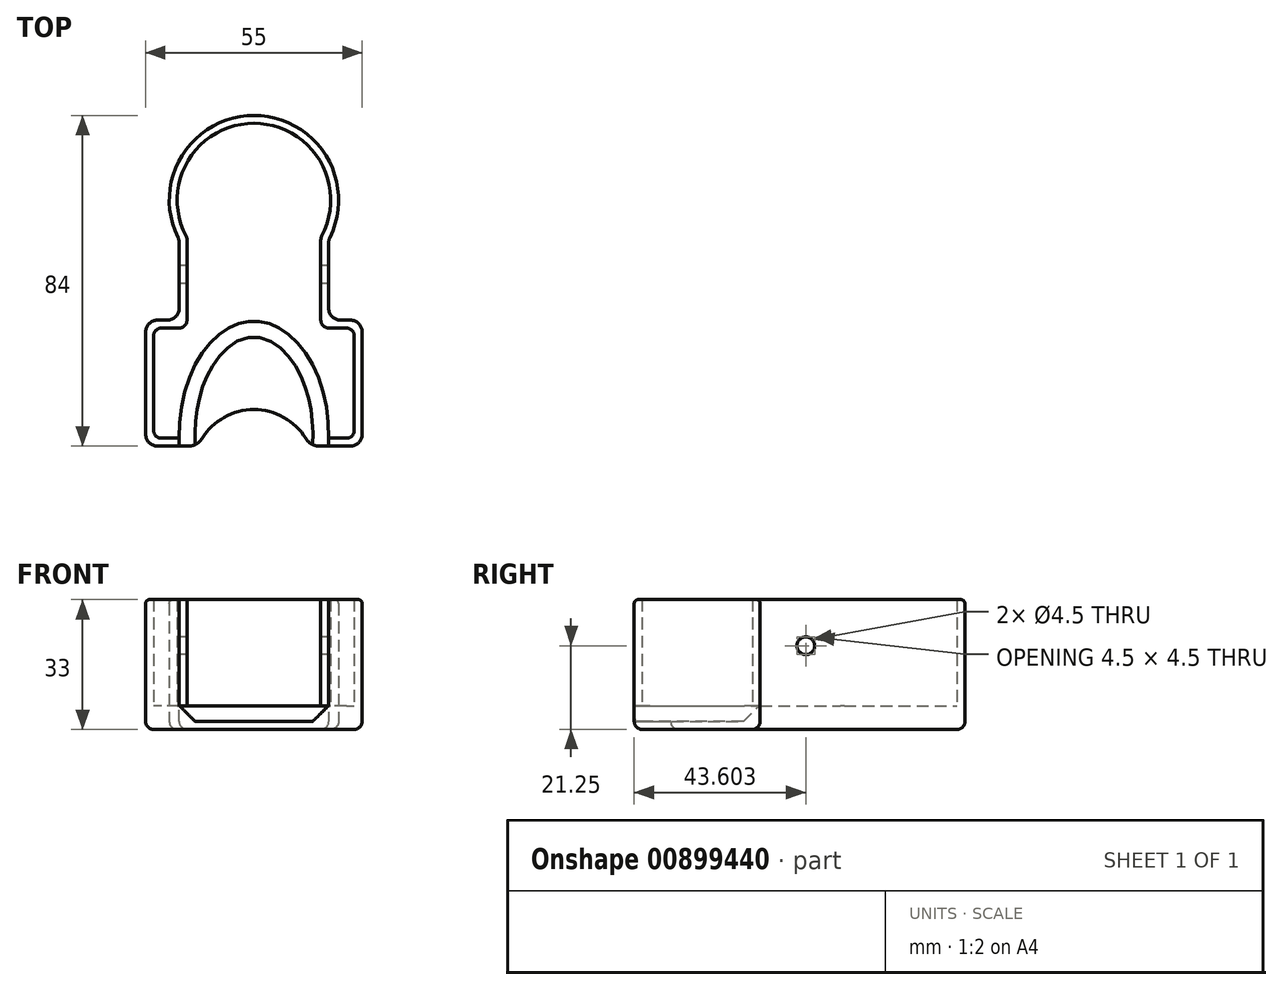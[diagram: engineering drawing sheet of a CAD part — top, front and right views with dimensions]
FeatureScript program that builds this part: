
annotation { "Feature Type Name" : "Feature", "Feature Type Description" : "" }
export const myFeature = defineFeature(function(context is Context, id is Id, definition is map)
    precondition{}
    {
        {
            var Q0;
            Q0=qCreatedBy(makeId("Top.planeOp"),FACE);
            var sketch = newSketch(context, id + "F0", { "sketchPlane" : qUnion([Q0])});
            skArc(sketch, "E0", {"start": v(17, -9.55) * mm, "mid": v(0, 19.5) * mm, "end": v(-17, -9.55) * mm});
            skArc(sketch, "E1", {"start": v(19, -10.06) * mm, "mid": v(0, 21.5) * mm, "end": v(-19, -10.06) * mm});
            skPoint(sketch, "E2.middle", {"position": v(0, -23.16) * mm});
            skLineSegment(sketch, "E3.left", {"start": v(19, -10.06) * mm, "end": v(19, -30.5) * mm});
            skLineSegment(sketch, "E3.right", {"start": v(-19, -10.06) * mm, "end": v(-19, -30.5) * mm});
            skLineSegment(sketch, "E4.bottom", {"start": v(27.5, -30.5) * mm, "end": v(19, -30.5) * mm});
            skLineSegment(sketch, "E4.top", {"start": v(27.5, -62.5) * mm, "end": v(-27.5, -62.5) * mm});
            skLineSegment(sketch, "E4.left", {"start": v(27.5, -30.5) * mm, "end": v(27.5, -62.5) * mm});
            skLineSegment(sketch, "E4.right", {"start": v(-27.5, -30.5) * mm, "end": v(-27.5, -62.5) * mm});
            skPoint(sketch, "E4.middle", {"position": v(0, -46.5) * mm});
            skLineSegment(sketch, "E5", {"start": v(-39.92, 21.5) * mm, "end": v(44.93, 21.5) * mm, "construction": true});
            skLineSegment(sketch, "E6.bottom", {"start": v(25.5, -60.5) * mm, "end": v(-25.5, -60.5) * mm});
            skLineSegment(sketch, "E6.top", {"start": v(25.5, -32.5) * mm, "end": v(17, -32.5) * mm});
            skLineSegment(sketch, "E6.left", {"start": v(25.5, -60.5) * mm, "end": v(25.5, -32.5) * mm});
            skLineSegment(sketch, "E6.right", {"start": v(-25.5, -60.5) * mm, "end": v(-25.5, -32.5) * mm});
            skLineSegment(sketch, "E7.trimOffspring", {"start": v(-19, -30.5) * mm, "end": v(-27.5, -30.5) * mm});
            skLineSegment(sketch, "E8.trimOffspring", {"start": v(-17, -32.5) * mm, "end": v(-25.5, -32.5) * mm});
            skLineSegment(sketch, "E9", {"start": v(-17, -32.5) * mm, "end": v(-17, -9.55) * mm});
            skLineSegment(sketch, "E10", {"start": v(17, -32.5) * mm, "end": v(17, -9.55) * mm});
            skSolve(sketch);
        }
        {
            var Q0;
            Q0 = qSketchRegion(id + "F0", true);
            extrude(context, id + "F1", {"entities" : qUnion([Q0]), "depth" : 27 * mm, "offsetDistance" : 25 * mm});
        }
        {
            var Q0;
            Q0=qCreatedBy(makeId("Top.planeOp"),FACE);
            var sketch = newSketch(context, id + "F2", { "sketchPlane" : qUnion([Q0])});
            skArc(sketch, "E11", {"start": v(19, -10.06) * mm, "mid": v(0, 21.5) * mm, "end": v(-19, -10.06) * mm});
            skPoint(sketch, "E12.middle", {"position": v(0, -23.16) * mm});
            skLineSegment(sketch, "E13.left", {"start": v(19, -10.06) * mm, "end": v(19, -30.5) * mm});
            skLineSegment(sketch, "E13.right", {"start": v(-19, -10.06) * mm, "end": v(-19, -30.5) * mm});
            skLineSegment(sketch, "E14.bottom", {"start": v(27.5, -30.5) * mm, "end": v(19, -30.5) * mm});
            skLineSegment(sketch, "E14.top", {"start": v(27.5, -62.5) * mm, "end": v(-27.5, -62.5) * mm});
            skLineSegment(sketch, "E14.left", {"start": v(27.5, -30.5) * mm, "end": v(27.5, -62.5) * mm});
            skLineSegment(sketch, "E14.right", {"start": v(-27.5, -30.5) * mm, "end": v(-27.5, -62.5) * mm});
            skPoint(sketch, "E14.middle", {"position": v(0, -46.5) * mm});
            skLineSegment(sketch, "E15.trimOffspring", {"start": v(-19, -30.5) * mm, "end": v(-27.5, -30.5) * mm});
            skSolve(sketch);
        }
        {
            var Q0;
            Q0 = qSketchRegion(id + "F2", true);
            extrude(context, id + "F3", {"entities" : qUnion([Q0]), "operationType" : NewBodyOperationType.ADD, "oppositeDirection" : true, "depth" : 6 * mm, "offsetDistance" : 25 * mm});
        }
        {
            var Q0;
            Q0=qCreatedBy(makeId("Top.planeOp"),FACE);
            var sketch = newSketch(context, id + "F4", { "sketchPlane" : qUnion([Q0])});
            skLineSegment(sketch, "E16", {"start": v(49.02, 21.5) * mm, "end": v(-41.67, 21.5) * mm, "construction": true});
            skEllipse(sketch, "E17", {"center": v(0, -60) * mm, "majorRadius": 31 * mm, "minorRadius": 21 * mm, "majorAxis": v(0, 1)});
            skSolve(sketch);
        }
        {
            var Q0;
            Q0 = qSketchRegion(id + "F4", true);
            extrude(context, id + "F5", {"entities" : qUnion([Q0]), "operationType" : NewBodyOperationType.ADD, "oppositeDirection" : true, "depth" : 6 * mm, "offsetDistance" : 25 * mm});
        }
        {
            var Q0;
            Q0=qCreatedBy(makeId("Top.planeOp"),FACE);
            var sketch = newSketch(context, id + "F6", { "sketchPlane" : qUnion([Q0])});
            skEllipse(sketch, "E18", {"center": v(0, -59.78) * mm, "majorRadius": 29 * mm, "minorRadius": 19 * mm, "majorAxis": v(0, 1)});
            skSolve(sketch);
        }
        {
            var Q0;
            Q0 = qSketchRegion(id + "F6", true);
            extrude(context, id + "F7", {"entities" : qUnion([Q0]), "operationType" : NewBodyOperationType.REMOVE, "oppositeDirection" : true, "depth" : 4 * mm, "offsetDistance" : 25 * mm});
        }
        {
            var Q0;
            Q0=makeQuery(id+"F7.boolean.opBoolean","COPY",EDGE,{"derivedFrom":makeQuery(id+"F7.opExtrude","CAP_EDGE",EDGE,{"disambiguationData":[OSD([sQuery(id+"F6.wireOp",EDGE,"E18")])],"isStart":false})});
            chamfer(context, id + "F8", {"entities" : qUnion([Q0]), "width" : 4 * mm, "tangentPropagation" : true});
        }
        {
            var Q0;
            Q0=makeQuery(id+"F5.opExtrude","CAP_EDGE",EDGE,{"disambiguationData":[OSD([sQuery(id+"F4.wireOp",EDGE,"E17")])],"isStart":false});
            chamfer(context, id + "F9", {"entities" : qUnion([Q0]), "width" : 6 * mm, "tangentPropagation" : true});
        }
        {
            var Q0;
            Q0=qCreatedBy(makeId("Top.planeOp"),FACE);
            var sketch = newSketch(context, id + "F10", { "sketchPlane" : qUnion([Q0])});
            skLineSegment(sketch, "E19", {"start": v(-36.83, 21.5) * mm, "end": v(59.05, 21.5) * mm, "construction": true});
            skLineSegment(sketch, "E20.bottom", {"start": v(-18.92, -94.76) * mm, "end": v(18.92, -94.76) * mm});
            skLineSegment(sketch, "E20.left", {"start": v(-18.92, -94.76) * mm, "end": v(-18.92, -62.5) * mm});
            skLineSegment(sketch, "E20.right", {"start": v(18.92, -94.76) * mm, "end": v(18.92, -62.5) * mm});
            skPoint(sketch, "E20.middle", {"position": v(0, -78.63) * mm});
            skLineSegment(sketch, "E21.bottom", {"start": v(18.92, -62.5) * mm, "end": v(-18.92, -62.5) * mm});
            skLineSegment(sketch, "E22.bottom", {"start": v(18.92, -62.5) * mm, "end": v(22.92, -62.5) * mm});
            skLineSegment(sketch, "E22.top", {"start": v(18.92, -75.28) * mm, "end": v(22.92, -75.28) * mm});
            skLineSegment(sketch, "E22.left", {"start": v(18.92, -62.5) * mm, "end": v(18.92, -75.28) * mm});
            skLineSegment(sketch, "E22.right", {"start": v(22.92, -62.5) * mm, "end": v(22.92, -75.28) * mm});
            skLineSegment(sketch, "E23.bottom", {"start": v(-18.92, -62.5) * mm, "end": v(-22.65, -62.5) * mm});
            skLineSegment(sketch, "E23.top", {"start": v(-18.92, -75.28) * mm, "end": v(-22.65, -75.28) * mm});
            skLineSegment(sketch, "E23.left", {"start": v(-18.92, -62.5) * mm, "end": v(-18.92, -75.28) * mm});
            skLineSegment(sketch, "E23.right", {"start": v(-22.65, -62.5) * mm, "end": v(-22.65, -75.28) * mm});
            skSolve(sketch);
        }
        {
            var Q0;
            Q0 = qSketchRegion(id + "F10", true);
            var Q1;
            Q1=makeQuery(id+"F3.opExtrude","CAP_FACE",FACE,{"disambiguationData":[OSD([sQuery(id+"F2.wireOp",EDGE,"E11"),sQuery(id+"F2.wireOp",EDGE,"E13.left"),sQuery(id+"F2.wireOp",EDGE,"E13.right"),sQuery(id+"F2.wireOp",EDGE,"E14.bottom"),sQuery(id+"F2.wireOp",EDGE,"E14.top"),sQuery(id+"F2.wireOp",EDGE,"E14.left"),sQuery(id+"F2.wireOp",EDGE,"E14.right"),sQuery(id+"F2.wireOp",EDGE,"E15.trimOffspring")])],"isStart":false});
            var Q2;
            Q2=makeQuery(id+"F1.opExtrude","CAP_FACE",FACE,{"disambiguationData":[OSD([sQuery(id+"F0.wireOp",EDGE,"E0"),sQuery(id+"F0.wireOp",EDGE,"E1"),sQuery(id+"F0.wireOp",EDGE,"E3.left"),sQuery(id+"F0.wireOp",EDGE,"E3.right"),sQuery(id+"F0.wireOp",EDGE,"E4.bottom"),sQuery(id+"F0.wireOp",EDGE,"E4.top"),sQuery(id+"F0.wireOp",EDGE,"E4.left"),sQuery(id+"F0.wireOp",EDGE,"E4.right"),sQuery(id+"F0.wireOp",EDGE,"E6.bottom"),sQuery(id+"F0.wireOp",EDGE,"E6.top"),sQuery(id+"F0.wireOp",EDGE,"E6.left"),sQuery(id+"F0.wireOp",EDGE,"E6.right"),sQuery(id+"F0.wireOp",EDGE,"E7.trimOffspring"),sQuery(id+"F0.wireOp",EDGE,"E8.trimOffspring"),sQuery(id+"F0.wireOp",EDGE,"E9"),sQuery(id+"F0.wireOp",EDGE,"E10")])],"isStart":false});
            extrude(context, id + "F11", {"entities" : qUnion([Q0]), "operationType" : NewBodyOperationType.REMOVE, "oppositeDirection" : true, "depth" : 25 * mm, "endBoundEntityFace" : qUnion([Q1]), "offsetDistance" : 25 * mm, "hasSecondDirection" : true, "secondDirectionOppositeDirection" : false, "secondDirectionDepth" : 30 * mm, "secondDirectionBoundEntityFace" : qUnion([Q2])});
        }
        {
            var Q0;
            Q0=qCreatedBy(makeId("Top.planeOp"),FACE);
            var sketch = newSketch(context, id + "F12", { "sketchPlane" : qUnion([Q0])});
            skLineSegment(sketch, "E24.bottom", {"start": v(-19, -60.5) * mm, "end": v(19, -60.5) * mm});
            skLineSegment(sketch, "E24.top", {"start": v(-19, -62.5) * mm, "end": v(19, -62.5) * mm});
            skLineSegment(sketch, "E24.left", {"start": v(-19, -60.5) * mm, "end": v(-19, -62.5) * mm});
            skLineSegment(sketch, "E24.right", {"start": v(19, -60.5) * mm, "end": v(19, -62.5) * mm});
            skPoint(sketch, "E24.middle", {"position": v(0, -61.5) * mm});
            skSolve(sketch);
        }
        {
            var Q0;
            Q0 = qSketchRegion(id + "F12", true);
            extrude(context, id + "F13", {"entities" : qUnion([Q0]), "operationType" : NewBodyOperationType.REMOVE, "depth" : 30 * mm, "offsetDistance" : 25 * mm});
        }
        {
            var Q0;
            Q0=makeQuery(id+"F5.opExtrude","CAP_FACE",FACE,{"disambiguationData":[OSD([sQuery(id+"F4.wireOp",EDGE,"E17")])],"isStart":false});
            var sketch = newSketch(context, id + "F14", { "sketchPlane" : qUnion([Q0])});
            skCircle(sketch, "E25", {"center": v(0, 68.72) * mm, "radius": 15.5 * mm});
            skLineSegment(sketch, "E26", {"start": v(-15.5, 16.16) * mm, "end": v(-15.5, 72.02) * mm, "construction": true});
            skSolve(sketch);
        }
        {
            var Q0;
            Q0 = qSketchRegion(id + "F14", true);
            var Q1;
            Q1=makeQuery(id+"F7.boolean.opBoolean","COPY",FACE,{"derivedFrom":makeQuery(id+"F7.opExtrude","CAP_FACE",FACE,{"disambiguationData":[OSD([sQuery(id+"F6.wireOp",EDGE,"E18")])],"isStart":false})});
            extrude(context, id + "F15", {"entities" : qUnion([Q0]), "operationType" : NewBodyOperationType.REMOVE, "endBound" : BoundingType.UP_TO_SURFACE, "oppositeDirection" : true, "depth" : 25 * mm, "endBoundEntityFace" : qUnion([Q1]), "offsetDistance" : 25 * mm});
        }
        {
            var Q0;
            Q0=makeQuery(id+"F15.boolean.opBoolean","INTERSECT",EDGE,{"disambiguationData":[OD(0.0)],"derivedFrom":[makeQuery(id+"F11.boolean.opBoolean","COPY",FACE,{"derivedFrom":makeQuery(id+"F11.opExtrude","SWEPT_FACE",FACE,{"disambiguationData":[OSD([sQuery(id+"F10.wireOp",EDGE,"E21.bottom"),sQuery(id+"F10.wireOp",EDGE,"E22.bottom"),sQuery(id+"F10.wireOp",EDGE,"E23.bottom")])]})}),makeQuery(id+"F15.opExtrude","SWEPT_FACE",FACE,{"disambiguationData":[OSD([sQuery(id+"F14.wireOp",EDGE,"E25")])]})]});
            var Q1;
            Q1=makeQuery(id+"F15.boolean.opBoolean","INTERSECT",EDGE,{"disambiguationData":[OD(1.0)],"derivedFrom":[makeQuery(id+"F11.boolean.opBoolean","COPY",FACE,{"derivedFrom":makeQuery(id+"F11.opExtrude","SWEPT_FACE",FACE,{"disambiguationData":[OSD([sQuery(id+"F10.wireOp",EDGE,"E21.bottom"),sQuery(id+"F10.wireOp",EDGE,"E22.bottom"),sQuery(id+"F10.wireOp",EDGE,"E23.bottom")])]})}),makeQuery(id+"F15.opExtrude","SWEPT_FACE",FACE,{"disambiguationData":[OSD([sQuery(id+"F14.wireOp",EDGE,"E25")])]})]});
            fillet(context, id + "F16", {"entities" : qUnion([Q0, Q1]), "radius" : 4 * mm, "tangentPropagation" : true, "allowEdgeOverflow" : false});
        }
        {
            var Q0;
            Q0=makeQuery(id+"F3.boolean.opBoolean","MERGE",EDGE,{"derivedFrom":[makeQuery(id+"F1.opExtrude","SWEPT_EDGE",EDGE,{"disambiguationData":[OSD([sQuery(id+"F0.wireOp",EDGE,"E4.top"),sQuery(id+"F0.wireOp",EDGE,"E4.left")])]}),makeQuery(id+"F3.opExtrude","SWEPT_EDGE",EDGE,{"disambiguationData":[OSD([sQuery(id+"F2.wireOp",EDGE,"E14.top"),sQuery(id+"F2.wireOp",EDGE,"E14.left")])]})]});
            var Q1;
            Q1=makeQuery(id+"F3.boolean.opBoolean","MERGE",EDGE,{"derivedFrom":[makeQuery(id+"F1.opExtrude","SWEPT_EDGE",EDGE,{"disambiguationData":[OSD([sQuery(id+"F0.wireOp",EDGE,"E4.bottom"),sQuery(id+"F0.wireOp",EDGE,"E4.left")])]}),makeQuery(id+"F3.opExtrude","SWEPT_EDGE",EDGE,{"disambiguationData":[OSD([sQuery(id+"F2.wireOp",EDGE,"E14.bottom"),sQuery(id+"F2.wireOp",EDGE,"E14.left")])]})]});
            var Q2;
            Q2=makeQuery(id+"F3.boolean.opBoolean","MERGE",EDGE,{"derivedFrom":[makeQuery(id+"F1.opExtrude","SWEPT_EDGE",EDGE,{"disambiguationData":[OSD([sQuery(id+"F0.wireOp",EDGE,"E3.left"),sQuery(id+"F0.wireOp",EDGE,"E4.bottom")])]}),makeQuery(id+"F3.opExtrude","SWEPT_EDGE",EDGE,{"disambiguationData":[OSD([sQuery(id+"F2.wireOp",EDGE,"E13.left"),sQuery(id+"F2.wireOp",EDGE,"E14.bottom")])]})]});
            var Q3;
            Q3=makeQuery(id+"F3.boolean.opBoolean","MERGE",EDGE,{"derivedFrom":[makeQuery(id+"F1.opExtrude","SWEPT_EDGE",EDGE,{"disambiguationData":[OSD([sQuery(id+"F0.wireOp",EDGE,"E1"),sQuery(id+"F0.wireOp",EDGE,"E3.left")])]}),makeQuery(id+"F3.opExtrude","SWEPT_EDGE",EDGE,{"disambiguationData":[OSD([sQuery(id+"F2.wireOp",EDGE,"E11"),sQuery(id+"F2.wireOp",EDGE,"E13.left")])]})]});
            var Q4;
            Q4=makeQuery(id+"F3.boolean.opBoolean","MERGE",EDGE,{"derivedFrom":[makeQuery(id+"F1.opExtrude","SWEPT_EDGE",EDGE,{"disambiguationData":[OSD([sQuery(id+"F0.wireOp",EDGE,"E1"),sQuery(id+"F0.wireOp",EDGE,"E3.right")])]}),makeQuery(id+"F3.opExtrude","SWEPT_EDGE",EDGE,{"disambiguationData":[OSD([sQuery(id+"F2.wireOp",EDGE,"E11"),sQuery(id+"F2.wireOp",EDGE,"E13.right")])]})]});
            var Q5;
            Q5=makeQuery(id+"F3.boolean.opBoolean","MERGE",EDGE,{"derivedFrom":[makeQuery(id+"F1.opExtrude","SWEPT_EDGE",EDGE,{"disambiguationData":[OSD([sQuery(id+"F0.wireOp",EDGE,"E3.right"),sQuery(id+"F0.wireOp",EDGE,"E7.trimOffspring")])]}),makeQuery(id+"F3.opExtrude","SWEPT_EDGE",EDGE,{"disambiguationData":[OSD([sQuery(id+"F2.wireOp",EDGE,"E13.right"),sQuery(id+"F2.wireOp",EDGE,"E15.trimOffspring")])]})]});
            var Q6;
            Q6=makeQuery(id+"F3.boolean.opBoolean","MERGE",EDGE,{"derivedFrom":[makeQuery(id+"F1.opExtrude","SWEPT_EDGE",EDGE,{"disambiguationData":[OSD([sQuery(id+"F0.wireOp",EDGE,"E4.right"),sQuery(id+"F0.wireOp",EDGE,"E7.trimOffspring")])]}),makeQuery(id+"F3.opExtrude","SWEPT_EDGE",EDGE,{"disambiguationData":[OSD([sQuery(id+"F2.wireOp",EDGE,"E14.right"),sQuery(id+"F2.wireOp",EDGE,"E15.trimOffspring")])]})]});
            var Q7;
            Q7=makeQuery(id+"F3.boolean.opBoolean","MERGE",EDGE,{"derivedFrom":[makeQuery(id+"F1.opExtrude","SWEPT_EDGE",EDGE,{"disambiguationData":[OSD([sQuery(id+"F0.wireOp",EDGE,"E4.top"),sQuery(id+"F0.wireOp",EDGE,"E4.right")])]}),makeQuery(id+"F3.opExtrude","SWEPT_EDGE",EDGE,{"disambiguationData":[OSD([sQuery(id+"F2.wireOp",EDGE,"E14.top"),sQuery(id+"F2.wireOp",EDGE,"E14.right")])]})]});
            fillet(context, id + "F17", {"entities" : qUnion([Q0, Q1, Q2, Q3, Q4, Q5, Q6, Q7]), "radius" : 3 * mm, "tangentPropagation" : true, "allowEdgeOverflow" : false});
        }
        {
            var Q0;
            Q0=makeQuery(id+"F1.opExtrude","SWEPT_EDGE",EDGE,{"disambiguationData":[OSD([sQuery(id+"F0.wireOp",EDGE,"E6.bottom"),sQuery(id+"F0.wireOp",EDGE,"E6.left")])]});
            var Q1;
            Q1=makeQuery(id+"F1.opExtrude","SWEPT_EDGE",EDGE,{"disambiguationData":[OSD([sQuery(id+"F0.wireOp",EDGE,"E6.top"),sQuery(id+"F0.wireOp",EDGE,"E6.left")])]});
            var Q2;
            Q2=makeQuery(id+"F1.opExtrude","SWEPT_EDGE",EDGE,{"disambiguationData":[OSD([sQuery(id+"F0.wireOp",EDGE,"E6.top"),sQuery(id+"F0.wireOp",EDGE,"E10")])]});
            var Q3;
            Q3=makeQuery(id+"F1.opExtrude","SWEPT_EDGE",EDGE,{"disambiguationData":[OSD([sQuery(id+"F0.wireOp",EDGE,"E0"),sQuery(id+"F0.wireOp",EDGE,"E10")])]});
            var Q4;
            Q4=makeQuery(id+"F1.opExtrude","SWEPT_EDGE",EDGE,{"disambiguationData":[OSD([sQuery(id+"F0.wireOp",EDGE,"E6.bottom"),sQuery(id+"F0.wireOp",EDGE,"E6.right")])]});
            var Q5;
            Q5=makeQuery(id+"F1.opExtrude","SWEPT_EDGE",EDGE,{"disambiguationData":[OSD([sQuery(id+"F0.wireOp",EDGE,"E8.trimOffspring"),sQuery(id+"F0.wireOp",EDGE,"E9")])]});
            var Q6;
            Q6=makeQuery(id+"F1.opExtrude","SWEPT_EDGE",EDGE,{"disambiguationData":[OSD([sQuery(id+"F0.wireOp",EDGE,"E0"),sQuery(id+"F0.wireOp",EDGE,"E9")])]});
            var Q7;
            Q7=makeQuery(id+"F1.opExtrude","SWEPT_EDGE",EDGE,{"disambiguationData":[OSD([sQuery(id+"F0.wireOp",EDGE,"E6.right"),sQuery(id+"F0.wireOp",EDGE,"E8.trimOffspring")])]});
            var Q8;
            Q8=makeQuery(id+"F1.opExtrude","CAP_EDGE",EDGE,{"disambiguationData":[OSD([sQuery(id+"F0.wireOp",EDGE,"E9")])],"isStart":true});
            var Q9;
            Q9=makeQuery(id+"F1.opExtrude","CAP_EDGE",EDGE,{"disambiguationData":[OSD([sQuery(id+"F0.wireOp",EDGE,"E6.right")])],"isStart":true});
            var Q10;
            Q10=makeQuery(id+"F1.opExtrude","CAP_EDGE",EDGE,{"disambiguationData":[OSD([sQuery(id+"F0.wireOp",EDGE,"E6.left")])],"isStart":true});
            fillet(context, id + "F18", {"entities" : qUnion([Q0, Q1, Q2, Q3, Q4, Q5, Q6, Q7, Q8, Q9, Q10]), "radius" : 2 * mm, "tangentPropagation" : true, "allowEdgeOverflow" : false});
        }
        {
            var Q0;
            Q0=makeQuery(id+"F1.opExtrude","CAP_EDGE",EDGE,{"disambiguationData":[OSD([sQuery(id+"F0.wireOp",EDGE,"E4.left")])],"isStart":false});
            fillet(context, id + "F19", {"entities" : qUnion([Q0]), "radius" : 1 * mm, "tangentPropagation" : true, "allowEdgeOverflow" : false});
        }
        {
            var Q0;
            Q0=makeQuery(id+"F3.opExtrude","CAP_EDGE",EDGE,{"disambiguationData":[OSD([sQuery(id+"F2.wireOp",EDGE,"E11")])],"isStart":false});
            fillet(context, id + "F20", {"entities" : qUnion([Q0]), "radius" : 2 * mm, "tangentPropagation" : true, "allowEdgeOverflow" : false});
        }
        {
            var Q0;
            Q0=qCreatedBy(makeId("Right.planeOp"),FACE);
            var sketch = newSketch(context, id + "F21", { "sketchPlane" : qUnion([Q0])});
            skCircle(sketch, "E27", {"center": v(-18.9, 15.25) * mm, "radius": 2.25 * mm});
            skSolve(sketch);
        }
        {
            var Q0;
            Q0 = qSketchRegion(id + "F21", true);
            var Q1;
            Q1=makeQuery(id+"F3.boolean.opBoolean","MERGE",FACE,{"derivedFrom":[makeQuery(id+"F1.opExtrude","SWEPT_FACE",FACE,{"disambiguationData":[OSD([sQuery(id+"F0.wireOp",EDGE,"E3.left")])]}),makeQuery(id+"F3.opExtrude","SWEPT_FACE",FACE,{"disambiguationData":[OSD([sQuery(id+"F2.wireOp",EDGE,"E13.left")])]})]});
            var Q2;
            Q2=makeQuery(id+"F3.boolean.opBoolean","MERGE",FACE,{"derivedFrom":[makeQuery(id+"F1.opExtrude","SWEPT_FACE",FACE,{"disambiguationData":[OSD([sQuery(id+"F0.wireOp",EDGE,"E3.right")])]}),makeQuery(id+"F3.opExtrude","SWEPT_FACE",FACE,{"disambiguationData":[OSD([sQuery(id+"F2.wireOp",EDGE,"E13.right")])]})]});
            extrude(context, id + "F22", {"entities" : qUnion([Q0]), "operationType" : NewBodyOperationType.REMOVE, "endBound" : BoundingType.UP_TO_SURFACE, "depth" : 25 * mm, "endBoundEntityFace" : qUnion([Q1]), "offsetDistance" : 25 * mm, "hasSecondDirection" : true, "secondDirectionBound" : SecondDirectionBoundingType.UP_TO_SURFACE, "secondDirectionOppositeDirection" : true, "secondDirectionDepth" : 25 * mm, "secondDirectionBoundEntityFace" : qUnion([Q2])});
        }
    });
